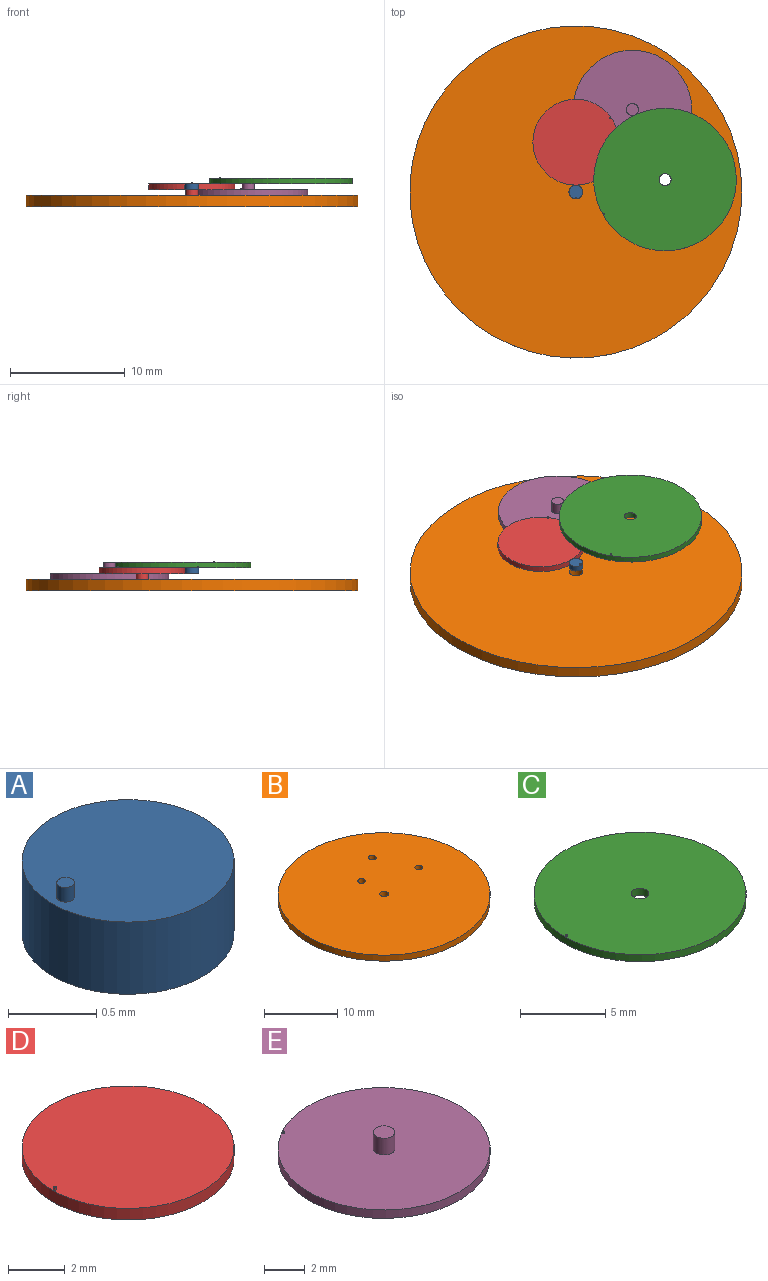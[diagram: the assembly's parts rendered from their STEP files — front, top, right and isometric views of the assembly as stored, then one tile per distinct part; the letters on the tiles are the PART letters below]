
ASSEMBLY  parts=5 mates=4
PART A: 5 faces, bbox 1.2x1.2x0.6 mm
  f0: cylinder r=0.6mm len=1.2mm, axis (0,0,-1), area 1.9mm2, adj f1,f2
  f1: plane 1.2x1.2mm, normal (0,0,1), area 1.1mm2, adj f0,f3
  f2: plane 1.2x1.2mm, normal (0,0,-1), area 1.1mm2, adj f0
  f3: cylinder r=0.05mm len=0.1mm, axis (0,0,-1), area 0mm2, adj f1,f4
  f4: plane 0.1x0.1mm, normal (0,0,1), area 0mm2, adj f3
PART B: 7 faces, bbox 29x29x1 mm
  f0: cylinder r=14.5mm len=29mm, axis (0,0,1), area 91.1mm2, adj f1,f2
  f1: plane 29x29mm, normal (0,0,-1), area 656.8mm2, adj f0,f3,f4,f5,f6
  f2: plane 29x29mm, normal (0,0,1), area 656.8mm2, adj f0,f3,f4,f5,f6
  f3: cylinder r=0.6mm len=1.2mm, axis (0,0,-1), area 3.8mm2, adj f1,f2
  f4: cylinder r=0.53mm len=1.05mm, axis (0,0,-1), area 3.3mm2, adj f1,f2
  f5: cylinder r=0.53mm len=1.05mm, axis (0,0,-1), area 3.3mm2, adj f1,f2
  f6: cylinder r=0.53mm len=1.05mm, axis (0,0,-1), area 3.3mm2, adj f1,f2
PART C: 6 faces, bbox 12.5x12.5x0.6 mm
  f0: cylinder r=6.22mm len=12.45mm, axis (0,0,-1), area 19.6mm2, adj f2,f3
  f1: cylinder r=0.53mm len=1.05mm, axis (0,0,-1), area 1.6mm2, adj f2,f3
  f2: plane 12.45x12.45mm, normal (0,0,1), area 120.9mm2, adj f0,f1,f4
  f3: plane 12.45x12.45mm, normal (0,0,-1), area 120.9mm2, adj f0,f1
  f4: cylinder r=0.05mm len=0.1mm, axis (0,0,-1), area 0mm2, adj f2,f5
  f5: plane 0.1x0.1mm, normal (0,0,1), area 0mm2, adj f4
PART D: 7 faces, bbox 7.5x7.5x2.1 mm
  f0: cylinder r=3.75mm len=7.5mm, axis (0,0,-1), area 11.8mm2, adj f1,f2
  f1: plane 7.5x7.5mm, normal (0,0,1), area 44.2mm2, adj f0,f5
  f2: plane 7.5x7.5mm, normal (0,0,-1), area 43.3mm2, adj f0,f3
  f3: cylinder r=0.53mm len=1.5mm, axis (0,0,1), area 4.9mm2, adj f2,f4
  f4: plane 1.05x1.05mm, normal (0,0,-1), area 0.9mm2, adj f3
  f5: cylinder r=0.05mm len=0.1mm, axis (0,0,-1), area 0mm2, adj f1,f6
  f6: plane 0.1x0.1mm, normal (0,0,1), area 0mm2, adj f5
PART E: 7 faces, bbox 10.4x10.4x1.5 mm
  f0: cylinder r=5.17mm len=10.35mm, axis (0,0,-1), area 16.3mm2, adj f1,f2
  f1: plane 10.35x10.35mm, normal (0,0,1), area 83.3mm2, adj f0,f3,f5
  f2: plane 10.35x10.35mm, normal (0,0,-1), area 84.1mm2, adj f0
  f3: cylinder r=0.53mm len=1.05mm, axis (0,0,-1), area 3.3mm2, adj f1,f4
  f4: plane 1.05x1.05mm, normal (0,0,1), area 0.9mm2, adj f3
  f5: cylinder r=0.05mm len=0.1mm, axis (0,0,-1), area 0mm2, adj f1,f6
  f6: plane 0.1x0.1mm, normal (0,0,1), area 0mm2, adj f5
PLACE A rot(axis=(0,0,1),95.6deg) t=(0,0,-1)mm
PLACE B at identity fixed
PLACE C rot(axis=(0,0,1),29.2deg) t=(1.52,-3.66,-1)mm
PLACE D rot(axis=(0,0,-1),144.9deg) t=(-2.5,7.91,-1)mm
PLACE E rot(axis=(0,0,1),142.5deg) t=(13.23,9.91,-1)mm
MATE revolute A.f0 <-> B.f0  axis (0,0,-1) through (0,0,-0.5)mm
MATE revolute B.f5 <-> E.f0  axis (0,0,1) through (4.94,7.2,-1)mm
MATE revolute C.f0 <-> B.f6  axis (0,0,-1) through (7.79,1.08,0)mm
MATE revolute D.f0 <-> B.f4  axis (0,0,-1) through (0,4.35,-0.5)mm
